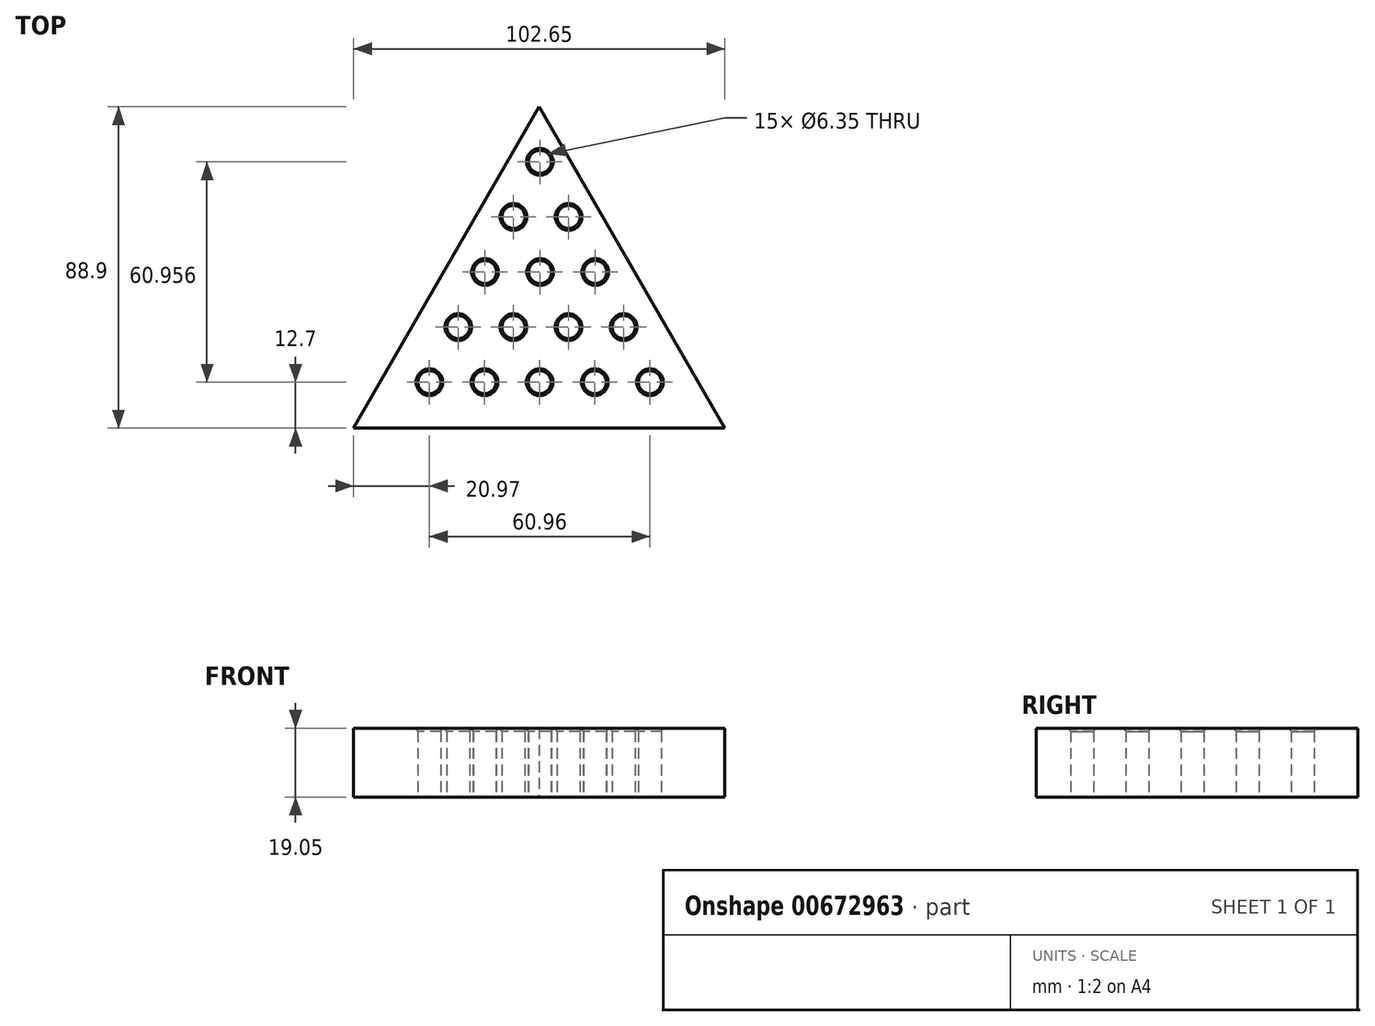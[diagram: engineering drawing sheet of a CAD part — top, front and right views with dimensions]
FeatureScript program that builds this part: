
annotation { "Feature Type Name" : "Feature", "Feature Type Description" : "" }
export const myFeature = defineFeature(function(context is Context, id is Id, definition is map)
    precondition{}
    {
        {
            var Q0;
            Q0=qCreatedBy(makeId("Top.planeOp"),FACE);
            var sketch = newSketch(context, id + "F0", { "sketchPlane" : qUnion([Q0])});
            skLineSegment(sketch, "E0.bottom", {"start": v(0, 0) * mm, "end": v(88.9, 0) * mm});
            skLineSegment(sketch, "E0.top", {"start": v(0, 88.9) * mm, "end": v(88.9, 88.9) * mm});
            skLineSegment(sketch, "E0.left", {"start": v(0, 0) * mm, "end": v(0, 88.9) * mm});
            skLineSegment(sketch, "E0.right", {"start": v(88.9, 0) * mm, "end": v(88.9, 88.9) * mm});
            skSolve(sketch);
        }
        {
            var Q0;
            Q0=makeQuery(id+"F0.imprint","IMPRINT",FACE,{"disambiguationData":[TD([[makeQuery(id+"F0.imprint","IMPRINT",EDGE,{"derivedFrom":sQuery(id+"F0.wireOp",EDGE,"E0.bottom")}),1.0]])]});
            var sketch = newSketch(context, id + "F1", { "sketchPlane" : qUnion([Q0])});
            skCircle(sketch, "E1", {"center": v(12.7, 12.7) * mm, "radius": 3.18 * mm});
            skCircle(sketch, "E2.1.0.0", {"center": v(27.94, 12.7) * mm, "radius": 3.18 * mm});
            skCircle(sketch, "E2.2.0.0", {"center": v(43.18, 12.7) * mm, "radius": 3.18 * mm});
            skCircle(sketch, "E2.3.0.0", {"center": v(58.42, 12.7) * mm, "radius": 3.18 * mm});
            skCircle(sketch, "E2.4.0.0", {"center": v(73.66, 12.7) * mm, "radius": 3.18 * mm});
            skLineSegment(sketch, "E2.direction1", {"start": v(12.7, 12.7) * mm, "end": v(27.94, 12.7) * mm, "construction": true});
            skSolve(sketch);
        }
        {
            var Q0;
            Q0=makeQuery(id+"F0.imprint","IMPRINT",FACE,{"disambiguationData":[TD([[makeQuery(id+"F0.imprint","IMPRINT",EDGE,{"derivedFrom":sQuery(id+"F0.wireOp",EDGE,"E0.bottom")}),1.0]])]});
            var sketch = newSketch(context, id + "F2", { "sketchPlane" : qUnion([Q0])});
            skCircle(sketch, "E3", {"center": v(20.67, 27.94) * mm, "radius": 3.18 * mm});
            skCircle(sketch, "E4.1.0.0", {"center": v(35.9, 27.94) * mm, "radius": 3.18 * mm});
            skCircle(sketch, "E4.2.0.0", {"center": v(51.15, 27.94) * mm, "radius": 3.18 * mm});
            skCircle(sketch, "E4.3.0.0", {"center": v(66.39, 27.94) * mm, "radius": 3.18 * mm});
            skLineSegment(sketch, "E4.direction1", {"start": v(20.67, 27.94) * mm, "end": v(35.9, 27.94) * mm, "construction": true});
            skSolve(sketch);
        }
        {
            var Q0;
            Q0=makeQuery(id+"F1.imprint","IMPRINT",FACE,{"disambiguationData":[TD([[makeQuery(id+"F1.imprint","IMPRINT",EDGE,{"derivedFrom":sQuery(id+"F1.wireOp",EDGE,"E1")}),-1.0]])]});
            var sketch = newSketch(context, id + "F3", { "sketchPlane" : qUnion([Q0])});
            skCircle(sketch, "E5", {"center": v(28.08, 43.18) * mm, "radius": 3.17 * mm});
            skCircle(sketch, "E6.1.0.0", {"center": v(43.32, 43.18) * mm, "radius": 3.17 * mm});
            skCircle(sketch, "E6.2.0.0", {"center": v(58.56, 43.18) * mm, "radius": 3.17 * mm});
            skLineSegment(sketch, "E6.direction1", {"start": v(28.08, 43.18) * mm, "end": v(43.32, 43.18) * mm, "construction": true});
            skSolve(sketch);
        }
        {
            var Q0;
            Q0=makeQuery(id+"F1.imprint","IMPRINT",FACE,{"disambiguationData":[TD([[makeQuery(id+"F1.imprint","IMPRINT",EDGE,{"derivedFrom":sQuery(id+"F1.wireOp",EDGE,"E1")}),-1.0]])]});
            var sketch = newSketch(context, id + "F4", { "sketchPlane" : qUnion([Q0])});
            skCircle(sketch, "E7", {"center": v(35.94, 58.42) * mm, "radius": 3.18 * mm});
            skCircle(sketch, "E8.1.0.0", {"center": v(51.18, 58.42) * mm, "radius": 3.18 * mm});
            skLineSegment(sketch, "E8.direction1", {"start": v(35.94, 58.42) * mm, "end": v(51.18, 58.42) * mm, "construction": true});
            skSolve(sketch);
        }
        {
            var Q0;
            Q0=makeQuery(id+"F2.imprint","IMPRINT",FACE,{"disambiguationData":[TD([[makeQuery(id+"F2.imprint","IMPRINT",EDGE,{"derivedFrom":sQuery(id+"F2.wireOp",EDGE,"E3")}),-1.0]])]});
            var sketch = newSketch(context, id + "F5", { "sketchPlane" : qUnion([Q0])});
            skCircle(sketch, "E9", {"center": v(43.23, 73.66) * mm, "radius": 3.17 * mm});
            skSolve(sketch);
        }
        {
            var Q0;
            Q0=makeQuery(id+"F1.imprint","IMPRINT",FACE,{"disambiguationData":[TD([[makeQuery(id+"F1.imprint","IMPRINT",EDGE,{"derivedFrom":sQuery(id+"F1.wireOp",EDGE,"E1")}),-1.0]])]});
            var sketch = newSketch(context, id + "F6", { "sketchPlane" : qUnion([Q0])});
            skCircle(sketch, "E10.cCircle", {"center": v(43.05, 29.63) * mm, "radius": 29.63 * mm, "construction": true});
            skLineSegment(sketch, "E10.0", {"start": v(94.38, 0) * mm, "end": v(-8.27, 0) * mm});
            skLineSegment(sketch, "E10.1", {"start": v(-8.27, 0) * mm, "end": v(43.05, 88.9) * mm});
            skLineSegment(sketch, "E10.2", {"start": v(43.05, 88.9) * mm, "end": v(94.38, 0) * mm});
            skPoint(sketch, "E10.0.midPoint", {"position": v(43.05, 0) * mm});
            skSolve(sketch);
        }
        {
            var Q0;
            Q0 = qSketchRegion(id + "F6", true);
            extrude(context, id + "F7", {"entities" : qUnion([Q0]), "depth" : 19.05 * mm, "offsetDistance" : 25.4 * mm});
        }
        {
            var Q0;
            Q0 = qSketchRegion(id + "F1", true);
            var Q1;
            Q1 = qSketchRegion(id + "F2", true);
            var Q2;
            Q2 = qSketchRegion(id + "F3", true);
            var Q3;
            Q3 = qSketchRegion(id + "F4", true);
            var Q4;
            Q4 = qSketchRegion(id + "F5", true);
            extrude(context, id + "F8", {"entities" : qUnion([Q0, Q1, Q2, Q3, Q4]), "operationType" : NewBodyOperationType.REMOVE, "depth" : 25.4 * mm, "offsetDistance" : 25.4 * mm});
        }
        {
            var Q0;
            Q0=makeQuery(id+"F8.boolean.opBoolean","INTERSECT",EDGE,{"derivedFrom":[makeQuery(id+"F7.opExtrude","CAP_FACE",FACE,{"disambiguationData":[OSD([sQuery(id+"F6.wireOp",EDGE,"E10.0"),sQuery(id+"F6.wireOp",EDGE,"E10.1"),sQuery(id+"F6.wireOp",EDGE,"E10.2")])],"isStart":false}),makeQuery(id+"F8.opExtrude","SWEPT_FACE",FACE,{"disambiguationData":[OSD([sQuery(id+"F1.wireOp",EDGE,"E1")])]})]});
            var Q1;
            Q1=makeQuery(id+"F8.boolean.opBoolean","INTERSECT",EDGE,{"derivedFrom":[makeQuery(id+"F7.opExtrude","CAP_FACE",FACE,{"disambiguationData":[OSD([sQuery(id+"F6.wireOp",EDGE,"E10.0"),sQuery(id+"F6.wireOp",EDGE,"E10.1"),sQuery(id+"F6.wireOp",EDGE,"E10.2")])],"isStart":false}),makeQuery(id+"F8.opExtrude","SWEPT_FACE",FACE,{"disambiguationData":[OSD([sQuery(id+"F1.wireOp",EDGE,"E2.1.0.0")])]})]});
            var Q2;
            Q2=makeQuery(id+"F8.boolean.opBoolean","INTERSECT",EDGE,{"derivedFrom":[makeQuery(id+"F7.opExtrude","CAP_FACE",FACE,{"disambiguationData":[OSD([sQuery(id+"F6.wireOp",EDGE,"E10.0"),sQuery(id+"F6.wireOp",EDGE,"E10.1"),sQuery(id+"F6.wireOp",EDGE,"E10.2")])],"isStart":false}),makeQuery(id+"F8.opExtrude","SWEPT_FACE",FACE,{"disambiguationData":[OSD([sQuery(id+"F1.wireOp",EDGE,"E2.2.0.0")])]})]});
            var Q3;
            Q3=makeQuery(id+"F8.boolean.opBoolean","INTERSECT",EDGE,{"derivedFrom":[makeQuery(id+"F7.opExtrude","CAP_FACE",FACE,{"disambiguationData":[OSD([sQuery(id+"F6.wireOp",EDGE,"E10.0"),sQuery(id+"F6.wireOp",EDGE,"E10.1"),sQuery(id+"F6.wireOp",EDGE,"E10.2")])],"isStart":false}),makeQuery(id+"F8.opExtrude","SWEPT_FACE",FACE,{"disambiguationData":[OSD([sQuery(id+"F1.wireOp",EDGE,"E2.3.0.0")])]})]});
            var Q4;
            Q4=makeQuery(id+"F8.boolean.opBoolean","INTERSECT",EDGE,{"derivedFrom":[makeQuery(id+"F7.opExtrude","CAP_FACE",FACE,{"disambiguationData":[OSD([sQuery(id+"F6.wireOp",EDGE,"E10.0"),sQuery(id+"F6.wireOp",EDGE,"E10.1"),sQuery(id+"F6.wireOp",EDGE,"E10.2")])],"isStart":false}),makeQuery(id+"F8.opExtrude","SWEPT_FACE",FACE,{"disambiguationData":[OSD([sQuery(id+"F1.wireOp",EDGE,"E2.4.0.0")])]})]});
            var Q5;
            Q5=makeQuery(id+"F8.boolean.opBoolean","INTERSECT",EDGE,{"derivedFrom":[makeQuery(id+"F7.opExtrude","CAP_FACE",FACE,{"disambiguationData":[OSD([sQuery(id+"F6.wireOp",EDGE,"E10.0"),sQuery(id+"F6.wireOp",EDGE,"E10.1"),sQuery(id+"F6.wireOp",EDGE,"E10.2")])],"isStart":false}),makeQuery(id+"F8.opExtrude","SWEPT_FACE",FACE,{"disambiguationData":[OSD([sQuery(id+"F2.wireOp",EDGE,"E4.3.0.0")])]})]});
            var Q6;
            Q6=makeQuery(id+"F8.boolean.opBoolean","INTERSECT",EDGE,{"derivedFrom":[makeQuery(id+"F7.opExtrude","CAP_FACE",FACE,{"disambiguationData":[OSD([sQuery(id+"F6.wireOp",EDGE,"E10.0"),sQuery(id+"F6.wireOp",EDGE,"E10.1"),sQuery(id+"F6.wireOp",EDGE,"E10.2")])],"isStart":false}),makeQuery(id+"F8.opExtrude","SWEPT_FACE",FACE,{"disambiguationData":[OSD([sQuery(id+"F2.wireOp",EDGE,"E4.2.0.0")])]})]});
            var Q7;
            Q7=makeQuery(id+"F8.boolean.opBoolean","INTERSECT",EDGE,{"derivedFrom":[makeQuery(id+"F7.opExtrude","CAP_FACE",FACE,{"disambiguationData":[OSD([sQuery(id+"F6.wireOp",EDGE,"E10.0"),sQuery(id+"F6.wireOp",EDGE,"E10.1"),sQuery(id+"F6.wireOp",EDGE,"E10.2")])],"isStart":false}),makeQuery(id+"F8.opExtrude","SWEPT_FACE",FACE,{"disambiguationData":[OSD([sQuery(id+"F2.wireOp",EDGE,"E4.1.0.0")])]})]});
            var Q8;
            Q8=makeQuery(id+"F8.boolean.opBoolean","INTERSECT",EDGE,{"derivedFrom":[makeQuery(id+"F7.opExtrude","CAP_FACE",FACE,{"disambiguationData":[OSD([sQuery(id+"F6.wireOp",EDGE,"E10.0"),sQuery(id+"F6.wireOp",EDGE,"E10.1"),sQuery(id+"F6.wireOp",EDGE,"E10.2")])],"isStart":false}),makeQuery(id+"F8.opExtrude","SWEPT_FACE",FACE,{"disambiguationData":[OSD([sQuery(id+"F2.wireOp",EDGE,"E3")])]})]});
            var Q9;
            Q9=makeQuery(id+"F8.boolean.opBoolean","INTERSECT",EDGE,{"derivedFrom":[makeQuery(id+"F7.opExtrude","CAP_FACE",FACE,{"disambiguationData":[OSD([sQuery(id+"F6.wireOp",EDGE,"E10.0"),sQuery(id+"F6.wireOp",EDGE,"E10.1"),sQuery(id+"F6.wireOp",EDGE,"E10.2")])],"isStart":false}),makeQuery(id+"F8.opExtrude","SWEPT_FACE",FACE,{"disambiguationData":[OSD([sQuery(id+"F3.wireOp",EDGE,"E5")])]})]});
            var Q10;
            Q10=makeQuery(id+"F8.boolean.opBoolean","INTERSECT",EDGE,{"derivedFrom":[makeQuery(id+"F7.opExtrude","CAP_FACE",FACE,{"disambiguationData":[OSD([sQuery(id+"F6.wireOp",EDGE,"E10.0"),sQuery(id+"F6.wireOp",EDGE,"E10.1"),sQuery(id+"F6.wireOp",EDGE,"E10.2")])],"isStart":false}),makeQuery(id+"F8.opExtrude","SWEPT_FACE",FACE,{"disambiguationData":[OSD([sQuery(id+"F3.wireOp",EDGE,"E6.1.0.0")])]})]});
            var Q11;
            Q11=makeQuery(id+"F8.boolean.opBoolean","INTERSECT",EDGE,{"derivedFrom":[makeQuery(id+"F7.opExtrude","CAP_FACE",FACE,{"disambiguationData":[OSD([sQuery(id+"F6.wireOp",EDGE,"E10.0"),sQuery(id+"F6.wireOp",EDGE,"E10.1"),sQuery(id+"F6.wireOp",EDGE,"E10.2")])],"isStart":false}),makeQuery(id+"F8.opExtrude","SWEPT_FACE",FACE,{"disambiguationData":[OSD([sQuery(id+"F3.wireOp",EDGE,"E6.2.0.0")])]})]});
            var Q12;
            Q12=makeQuery(id+"F8.boolean.opBoolean","INTERSECT",EDGE,{"derivedFrom":[makeQuery(id+"F7.opExtrude","CAP_FACE",FACE,{"disambiguationData":[OSD([sQuery(id+"F6.wireOp",EDGE,"E10.0"),sQuery(id+"F6.wireOp",EDGE,"E10.1"),sQuery(id+"F6.wireOp",EDGE,"E10.2")])],"isStart":false}),makeQuery(id+"F8.opExtrude","SWEPT_FACE",FACE,{"disambiguationData":[OSD([sQuery(id+"F4.wireOp",EDGE,"E8.1.0.0")])]})]});
            var Q13;
            Q13=makeQuery(id+"F8.boolean.opBoolean","INTERSECT",EDGE,{"derivedFrom":[makeQuery(id+"F7.opExtrude","CAP_FACE",FACE,{"disambiguationData":[OSD([sQuery(id+"F6.wireOp",EDGE,"E10.0"),sQuery(id+"F6.wireOp",EDGE,"E10.1"),sQuery(id+"F6.wireOp",EDGE,"E10.2")])],"isStart":false}),makeQuery(id+"F8.opExtrude","SWEPT_FACE",FACE,{"disambiguationData":[OSD([sQuery(id+"F4.wireOp",EDGE,"E7")])]})]});
            var Q14;
            Q14=makeQuery(id+"F8.boolean.opBoolean","INTERSECT",EDGE,{"derivedFrom":[makeQuery(id+"F7.opExtrude","CAP_FACE",FACE,{"disambiguationData":[OSD([sQuery(id+"F6.wireOp",EDGE,"E10.0"),sQuery(id+"F6.wireOp",EDGE,"E10.1"),sQuery(id+"F6.wireOp",EDGE,"E10.2")])],"isStart":false}),makeQuery(id+"F8.opExtrude","SWEPT_FACE",FACE,{"disambiguationData":[OSD([sQuery(id+"F5.wireOp",EDGE,"E9")])]})]});
            chamfer(context, id + "F9", {"entities" : qUnion([Q0, Q1, Q2, Q3, Q4, Q5, Q6, Q7, Q8, Q9, Q10, Q11, Q12, Q13, Q14]), "chamferType" : ChamferType.OFFSET_ANGLE, "width" : 0.5 * mm, "oppositeDirection" : false, "angle" : 60 * degree, "tangentPropagation" : true});
        }
    });
